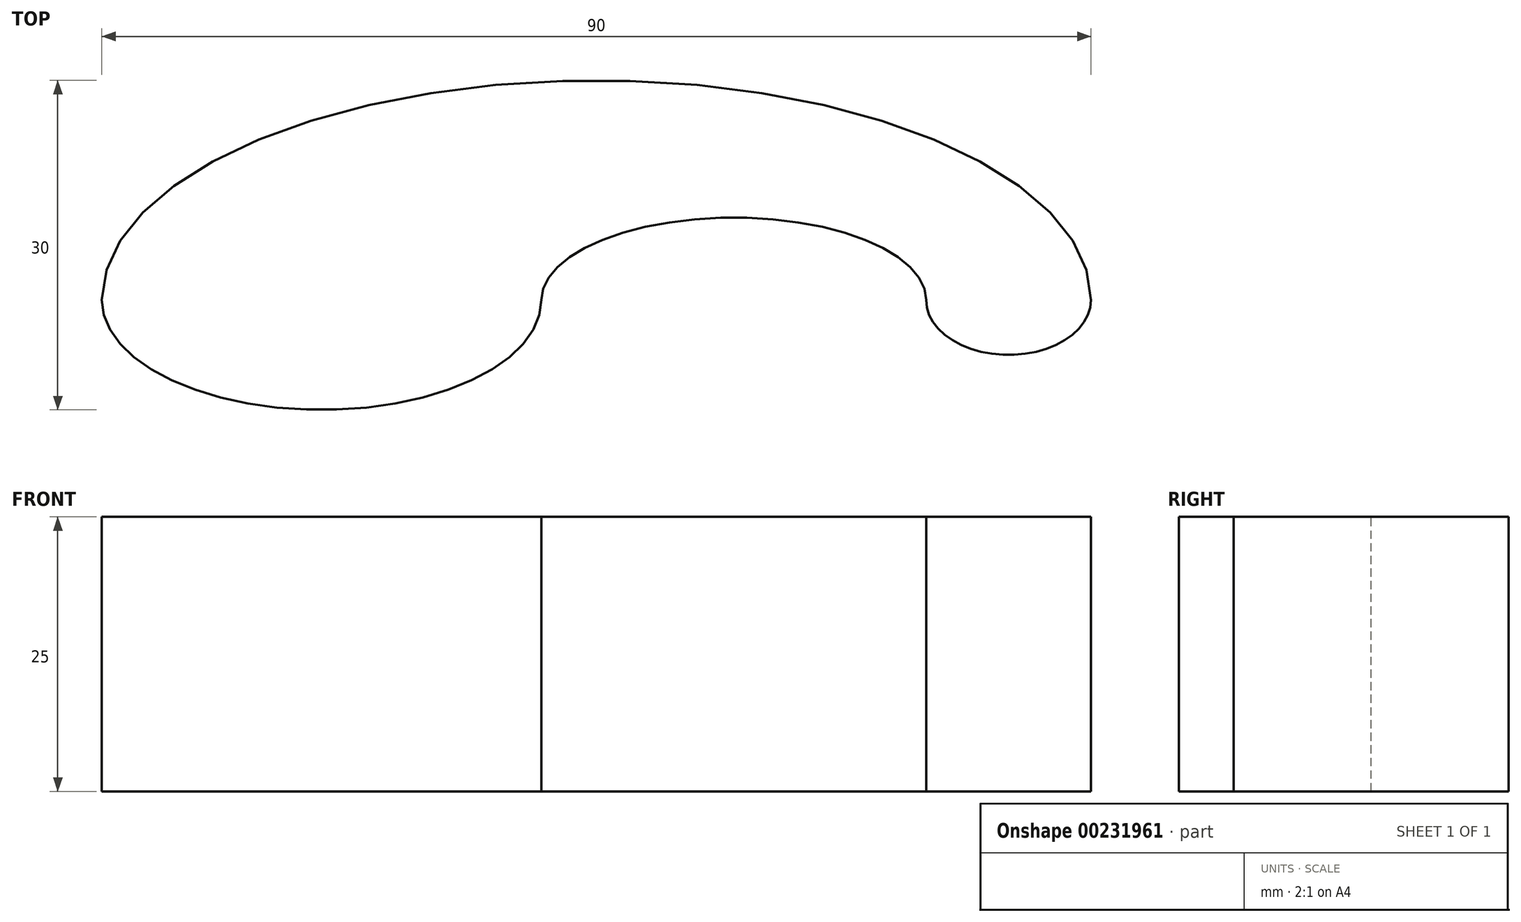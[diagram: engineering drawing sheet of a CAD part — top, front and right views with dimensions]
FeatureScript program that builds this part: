
annotation { "Feature Type Name" : "Feature", "Feature Type Description" : "" }
export const myFeature = defineFeature(function(context is Context, id is Id, definition is map)
    precondition{}
    {
        {
            var Q0;
            Q0=qCreatedBy(makeId("Top.planeOp"),FACE);
            var sketch = newSketch(context, id + "F0", { "sketchPlane" : qUnion([Q0])});
            skEllipticalArc(sketch, "E0", {});
            skEllipticalArc(sketch, "E1", {});
            skPoint(sketch, "E1.centerSnap0", {"position": v(20, 0) * mm});
            skEllipticalArc(sketch, "E2", {});
            skPoint(sketch, "E2.centerSnap0", {"position": v(55, 0) * mm});
            skLineSegment(sketch, "E3", {"start": v(-20, 0) * mm, "end": v(70, 0) * mm, "construction": true});
            skEllipticalArc(sketch, "E4", {});
            const initialGuessF0  = {"E0": [0, 0, 1, 0, 0.02, 0.01, 3.141592653589793, 0], "E1": [0.0375, 0, -1, 0, 0.0175, 0.0075, 3.141592653589793, 0], "E2": [0.0625, 0, -1, 0, 0.0075, 0.005, 0, 3.141592653589793], "E4": [0.025, 0, 1, 0, 0.045, 0.02, 0, 3.141592653589793]};
            skSetInitialGuess(sketch, initialGuessF0);
            skSolve(sketch);
        }
        {
            var Q0;
            Q0=makeQuery(id+"F0.imprint","IMPRINT",FACE,{"disambiguationData":[TD([[makeQuery(id+"F0.imprint","IMPRINT",EDGE,{"derivedFrom":sQuery(id+"F0.wireOp",EDGE,"E0")}),1.0]])]});
            extrude(context, id + "F1", {"entities" : qUnion([Q0]), "depth" : 25 * mm});
        }
    });
